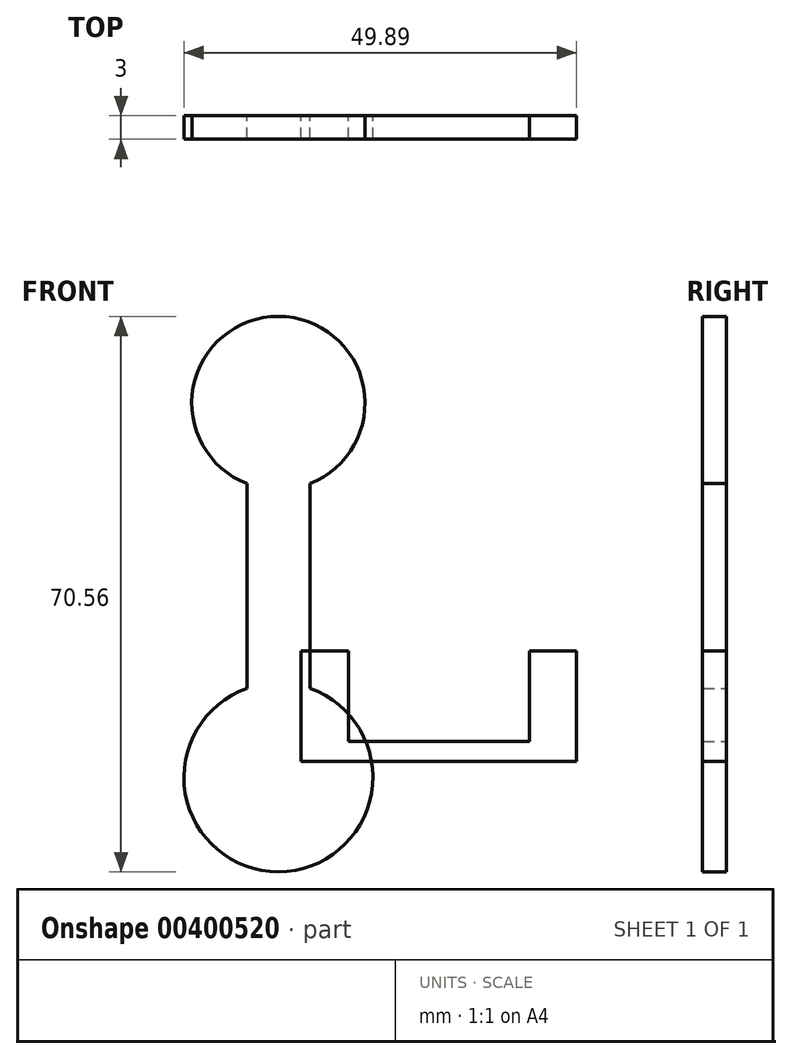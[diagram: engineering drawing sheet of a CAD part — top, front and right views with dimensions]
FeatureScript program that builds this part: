
annotation { "Feature Type Name" : "Feature", "Feature Type Description" : "" }
export const myFeature = defineFeature(function(context is Context, id is Id, definition is map)
    precondition{}
    {
        {
            var Q0;
            Q0=qCreatedBy(makeId("Front.planeOp"),FACE);
            var sketch = newSketch(context, id + "F0", { "sketchPlane" : qUnion([Q0])});
            skLineSegment(sketch, "E0", {"start": v(-29, -20.68) * mm, "end": v(6, -20.68) * mm});
            skLineSegment(sketch, "E1", {"start": v(6, -20.68) * mm, "end": v(6, -6.68) * mm});
            skLineSegment(sketch, "E2", {"start": v(6, -6.68) * mm, "end": v(0, -6.68) * mm});
            skLineSegment(sketch, "E3", {"start": v(0, -6.68) * mm, "end": v(0, -18.18) * mm});
            skLineSegment(sketch, "E4", {"start": v(0, -18.18) * mm, "end": v(-23, -18.18) * mm});
            skLineSegment(sketch, "E5", {"start": v(-23, -18.18) * mm, "end": v(-23, -6.68) * mm});
            skLineSegment(sketch, "E6", {"start": v(-29, -20.68) * mm, "end": v(-29, -6.67) * mm});
            skLineSegment(sketch, "E7", {"start": v(-29, -6.67) * mm, "end": v(-23, -6.68) * mm});
            skSolve(sketch);
        }
        {
            var Q0;
            Q0=makeQuery(id+"F0.imprint","IMPRINT",FACE,{"disambiguationData":[TD([[makeQuery(id+"F0.imprint","IMPRINT",EDGE,{"derivedFrom":sQuery(id+"F0.wireOp",EDGE,"E0")}),1.0]])]});
            extrude(context, id + "F1", {"entities" : qUnion([Q0]), "depth" : 3 * mm});
        }
        {
            var Q0;
            Q0=qCreatedBy(makeId("Front.planeOp"),FACE);
            var sketch = newSketch(context, id + "F2", { "sketchPlane" : qUnion([Q0])});
            skLineSegment(sketch, "E8.left", {"start": v(-35.9, 14.6) * mm, "end": v(-35.9, -11.4) * mm});
            skLineSegment(sketch, "E8.right", {"start": v(-27.9, 14.6) * mm, "end": v(-27.9, -11.4) * mm});
            skArc(sketch, "E9", {"start": v(-35.9, -11.4) * mm, "mid": v(-31.9, -34.72) * mm, "end": v(-27.9, -11.4) * mm});
            skArc(sketch, "E10", {"start": v(-27.9, 14.6) * mm, "mid": v(-31.9, 35.84) * mm, "end": v(-35.9, 14.6) * mm});
            skSolve(sketch);
        }
        {
            var Q0;
            Q0=makeQuery(id+"F2.imprint","IMPRINT",FACE,{"disambiguationData":[TD([[makeQuery(id+"F2.imprint","IMPRINT",EDGE,{"derivedFrom":sQuery(id+"F2.wireOp",EDGE,"E8.left")}),1.0]])]});
            extrude(context, id + "F3", {"entities" : qUnion([Q0]), "depth" : 3 * mm});
        }
    });
